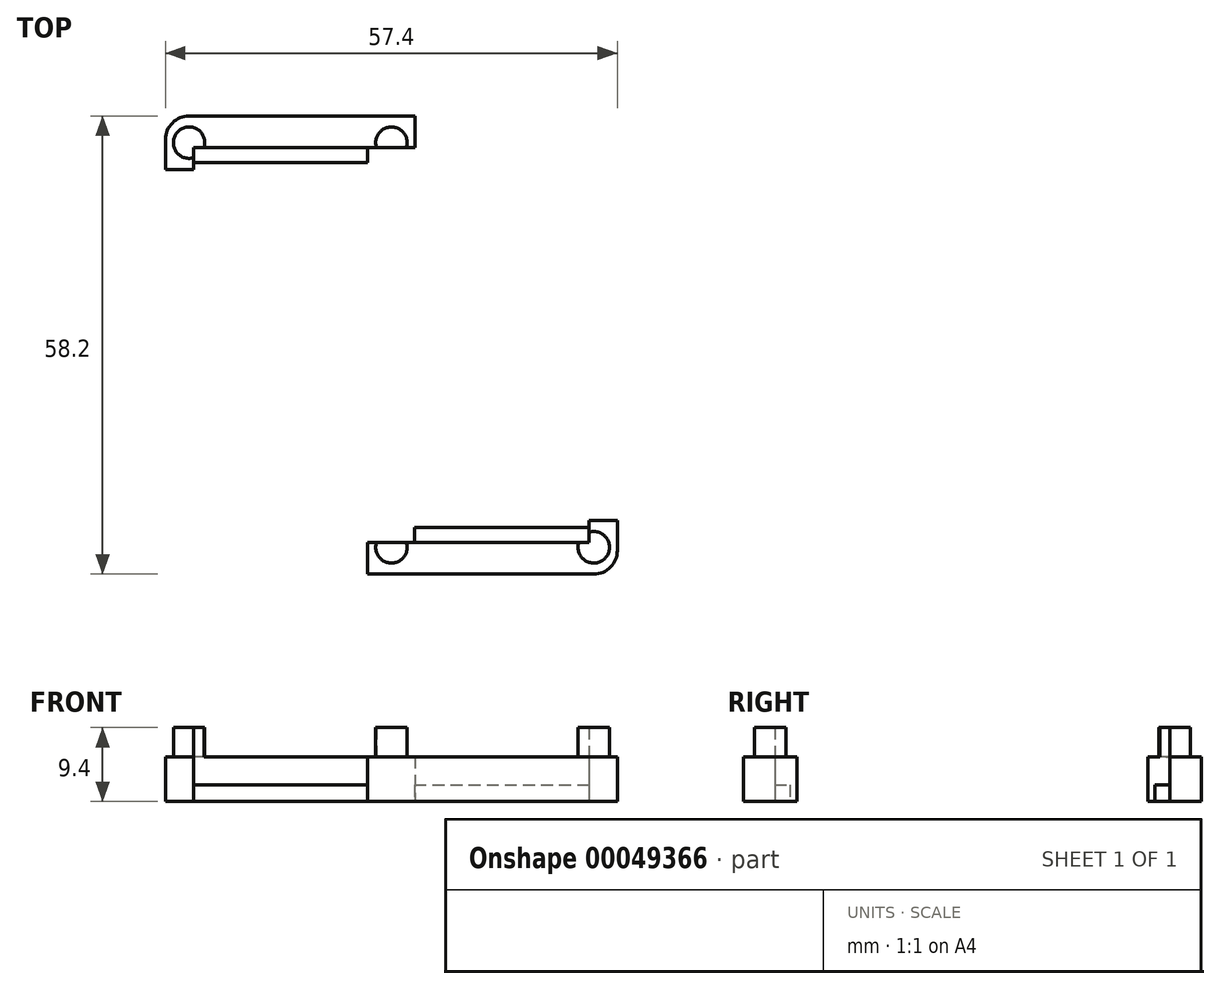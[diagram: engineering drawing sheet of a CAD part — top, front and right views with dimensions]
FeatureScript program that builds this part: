
annotation { "Feature Type Name" : "Feature", "Feature Type Description" : "" }
export const myFeature = defineFeature(function(context is Context, id is Id, definition is map)
    precondition{}
    {
        {
            var Q0;
            Q0=qCreatedBy(makeId("Top.planeOp"),FACE);
            var sketch = newSketch(context, id + "F0", { "sketchPlane" : qUnion([Q0])});
            skLineSegment(sketch, "E0.rect.top", {"start": v(24.8, 24.8) * mm, "end": v(24.03, 24.8) * mm});
            skLineSegment(sketch, "E0.rect.right", {"start": v(-24.8, -24.8) * mm, "end": v(-24.8, 22.3) * mm});
            skPoint(sketch, "E0.rect.middle", {"position": v(0, 0) * mm});
            skCircle(sketch, "E1", {"center": v(0, 0) * mm, "radius": 1.9 * mm});
            skCircle(sketch, "E2", {"center": v(25.7, 0) * mm, "radius": 1.9 * mm});
            skCircle(sketch, "E3", {"center": v(25.7, 25.7) * mm, "radius": 1.9 * mm});
            skPoint(sketch, "E4.MirrorP", {"position": v(0, 25.7) * mm});
            skCircle(sketch, "E5.MirrorC", {"center": v(-25.7, 0) * mm, "radius": 1.9 * mm});
            skArc(sketch, "E6.MirrorC", {"start": v(1.67, 24.8) * mm, "mid": v(0.16, 27.6) * mm, "end": v(-1.8, 25.1) * mm});
            skCircle(sketch, "E7.MirrorC", {"center": v(-25.7, -25.7) * mm, "radius": 1.9 * mm});
            skPoint(sketch, "E8.MirrorP", {"position": v(0, -25.7) * mm});
            skLineSegment(sketch, "E9.MirrorCS", {"start": v(-24.8, -24.8) * mm, "end": v(-3, -24.8) * mm});
            skLineSegment(sketch, "E10.MirrorCS", {"start": v(-3, -24.8) * mm, "end": v(-24.8, -24.8) * mm});
            skPoint(sketch, "E11.MirrorCS.end.orphan", {"position": v(-28.25, 12.85) * mm});
            skPoint(sketch, "E12.orphan", {"position": v(-25.7, 12.85) * mm});
            skPoint(sketch, "E13.endSnap0", {"position": v(0, -24.8) * mm});
            skLineSegment(sketch, "E14.rect.bottom", {"start": v(24.8, -22.3) * mm, "end": v(28.7, -22.3) * mm});
            skLineSegment(sketch, "E14.rect.top", {"start": v(-3, -29.1) * mm, "end": v(28.7, -29.1) * mm});
            skLineSegment(sketch, "E14.rect.left", {"start": v(-3, -24.8) * mm, "end": v(-3, -29.1) * mm});
            skLineSegment(sketch, "E14.rect.right", {"start": v(28.7, -22.3) * mm, "end": v(28.7, -29.1) * mm});
            skPoint(sketch, "E14.rect.middle", {"position": v(12.85, -25.7) * mm});
            skArc(sketch, "E15.MirrorCS", {"start": v(24.03, 24.8) * mm, "mid": v(27.04, 27.04) * mm, "end": v(24.8, 24.03) * mm});
            skArc(sketch, "E16.MirrorCS", {"start": v(24.8, 24.03) * mm, "mid": v(27.04, 27.04) * mm, "end": v(24.03, 24.8) * mm});
            skPoint(sketch, "E17.MirrorP", {"position": v(12.85, 25.7) * mm});
            skLineSegment(sketch, "E18.MirrorCS", {"start": v(-3, 29.1) * mm, "end": v(3, 29.1) * mm});
            skPoint(sketch, "E19.MirrorP", {"position": v(0, 24.8) * mm});
            skArc(sketch, "E20.MirrorC", {"start": v(1.8, 25.1) * mm, "mid": v(1.74, 24.95) * mm, "end": v(1.67, 24.8) * mm});
            skLineSegment(sketch, "E21.MirrorCS", {"start": v(-28.7, 22.3) * mm, "end": v(-28.7, 29.1) * mm});
            skLineSegment(sketch, "E22.MirrorCS", {"start": v(3, 29.1) * mm, "end": v(-28.7, 29.1) * mm});
            skLineSegment(sketch, "E23.MirrorCS", {"start": v(3, 24.8) * mm, "end": v(3, 29.1) * mm});
            skPoint(sketch, "E24.MirrorP", {"position": v(-12.85, 25.7) * mm});
            skArc(sketch, "E25.MirrorCS", {"start": v(1.67, 24.8) * mm, "mid": v(1.74, 24.95) * mm, "end": v(1.8, 25.1) * mm});
            skPoint(sketch, "E26.MirrorCS.end.orphan", {"position": v(28.7, 29.1) * mm});
            skPoint(sketch, "E27.orphan", {"position": v(28.7, 22.3) * mm});
            skPoint(sketch, "E28.end.orphan", {"position": v(-3.94, -25.7) * mm});
            skLineSegment(sketch, "E29", {"start": v(-3, -25.1) * mm, "end": v(-2.61, -25.1) * mm});
            skLineSegment(sketch, "E30", {"start": v(-2.61, -25.1) * mm, "end": v(25.13, -25.1) * mm});
            skLineSegment(sketch, "E31", {"start": v(25.13, -25.1) * mm, "end": v(25.13, -22.3) * mm});
            skLineSegment(sketch, "E32.trimOffspring", {"start": v(24.8, -22.3) * mm, "end": v(24.8, 24.8) * mm});
            skPoint(sketch, "E33.orphan", {"position": v(24.8, -24.03) * mm});
            skPoint(sketch, "E34.MirrorC.start.orphan", {"position": v(24.03, -24.8) * mm});
            skPoint(sketch, "E0.rect.bottom.start.orphan", {"position": v(24.8, -24.8) * mm});
            skPoint(sketch, "E35.orphan", {"position": v(-1.67, -24.8) * mm});
            skPoint(sketch, "E36.orphan", {"position": v(1.67, -24.8) * mm});
            skLineSegment(sketch, "E37", {"start": v(3, 25.1) * mm, "end": v(-25.12, 25.1) * mm});
            skLineSegment(sketch, "E38", {"start": v(-25.12, 25.1) * mm, "end": v(-25.12, 22.3) * mm});
            skPoint(sketch, "E39.orphan", {"position": v(-24.8, 24.8) * mm});
            skPoint(sketch, "E40.orphan", {"position": v(-24.8, 24.03) * mm});
            skPoint(sketch, "E41.MirrorC.center.orphan", {"position": v(-25.7, 25.7) * mm});
            skPoint(sketch, "E42.MirrorCS.end.orphan", {"position": v(-24.03, 24.8) * mm});
            skPoint(sketch, "E43.orphan", {"position": v(-1.67, 24.8) * mm});
            skLineSegment(sketch, "E44.trimOffspring", {"start": v(3, 24.8) * mm, "end": v(24.8, 24.8) * mm});
            skPoint(sketch, "E45.end.orphan", {"position": v(2.6, 25.1) * mm});
            skArc(sketch, "E46", {"start": v(-23.8, 25.1) * mm, "mid": v(-27.1, 27.12) * mm, "end": v(-25.12, 23.79) * mm});
            skCircle(sketch, "E47", {"center": v(0, 25.7) * mm, "radius": 2 * mm});
            skArc(sketch, "E48", {"start": v(-1.9, -25.1) * mm, "mid": v(0, -27.7) * mm, "end": v(1.9, -25.1) * mm});
            skArc(sketch, "E49", {"start": v(23.8, -25.1) * mm, "mid": v(27.1, -27.12) * mm, "end": v(25.13, -23.78) * mm});
            skLineSegment(sketch, "E50", {"start": v(2.92, -23.2) * mm, "end": v(25.13, -23.2) * mm});
            skLineSegment(sketch, "E51", {"start": v(2.92, -25.1) * mm, "end": v(2.92, -23.2) * mm});
            skPoint(sketch, "E52.start.orphan", {"position": v(-4.43, -22.3) * mm});
            skPoint(sketch, "E53.start.orphan", {"position": v(0, -22.3) * mm});
            skPoint(sketch, "E54.orphan", {"position": v(-3, -22.3) * mm});
            skLineSegment(sketch, "E55", {"start": v(-3, 23.2) * mm, "end": v(-3, 25.1) * mm});
            skLineSegment(sketch, "E56.trimOffspring", {"start": v(-24.8, 22.3) * mm, "end": v(-28.7, 22.3) * mm});
            skLineSegment(sketch, "E57.trimOffspring", {"start": v(-3, 23.2) * mm, "end": v(-25.12, 23.2) * mm});
            skPoint(sketch, "E58.start.orphan", {"position": v(4.08, 22.3) * mm});
            skPoint(sketch, "E59.MirrorCS.start.orphan", {"position": v(0, 22.3) * mm});
            skPoint(sketch, "E60.orphan", {"position": v(-3, 22.3) * mm});
            skPoint(sketch, "E61.MirrorCS.start.orphan", {"position": v(3, 22.3) * mm});
            skSolve(sketch);
        }
        {
            var Q0;
            {var subQ0=sQuery(id+"F0.wireOp",EDGE,"E49");Q0=makeQuery(id+"F0.imprint","IMPRINT",FACE,{"disambiguationData":[TD([[makeQuery(id+"F0.imprint","IMPRINT",EDGE,{"derivedFrom":subQ0}),1.0]])]});}
            var Q1;
            {var subQ0=sQuery(id+"F0.wireOp",EDGE,"E48");Q1=makeQuery(id+"F0.imprint","IMPRINT",FACE,{"disambiguationData":[TD([[makeQuery(id+"F0.imprint","IMPRINT",EDGE,{"derivedFrom":subQ0}),1.0]])]});}
            var Q2;
            {var subQ0=sQuery(id+"F0.wireOp",EDGE,"E46");Q2=makeQuery(id+"F0.imprint","IMPRINT",FACE,{"disambiguationData":[TD([[makeQuery(id+"F0.imprint","IMPRINT",EDGE,{"derivedFrom":subQ0}),1.0]])]});}
            var Q3;
            {var subQ1=sQuery(id+"F0.wireOp",EDGE,"E6.MirrorC");Q3=makeQuery(id+"F0.imprint","IMPRINT",FACE,{"disambiguationData":[TD([[makeQuery(id+"F0.imprint","IMPRINT",EDGE,{"derivedFrom":subQ1}),1.0]])]});}
            var Q4;
            {var subQ4=sQuery(id+"F0.wireOp",EDGE,"E6.MirrorC");Q4=makeQuery(id+"F0.imprint","IMPRINT",FACE,{"disambiguationData":[TD([[makeQuery(id+"F0.imprint","IMPRINT",EDGE,{"derivedFrom":subQ4}),-1.0]])]});}
            extrude(context, id + "F1", {"entities" : qUnion([Q0, Q1, Q2, Q3, Q4]), "depth" : 9.4 * mm});
        }
        {
            var Q0;
            {var subQ8=sQuery(id+"F0.wireOp",EDGE,"E14.rect.top");Q0=makeQuery(id+"F0.imprint","IMPRINT",FACE,{"disambiguationData":[TD([[makeQuery(id+"F0.imprint","IMPRINT",EDGE,{"derivedFrom":subQ8}),1.0]])]});}
            var Q1;
            {var subQ12=sQuery(id+"F0.wireOp",EDGE,"E21.MirrorCS");Q1=makeQuery(id+"F0.imprint","IMPRINT",FACE,{"disambiguationData":[TD([[makeQuery(id+"F0.imprint","IMPRINT",EDGE,{"derivedFrom":subQ12}),-1.0]])]});}
            extrude(context, id + "F2", {"entities" : qUnion([Q0, Q1]), "operationType" : NewBodyOperationType.ADD, "depth" : 5.7 * mm});
        }
        {
            var Q0;
            {var subQ1=sQuery(id+"F0.wireOp",EDGE,"E55");Q0=makeQuery(id+"F0.imprint","IMPRINT",FACE,{"disambiguationData":[TD([[makeQuery(id+"F0.imprint","IMPRINT",EDGE,{"derivedFrom":subQ1}),1.0]])]});}
            var Q1;
            {var subQ1=sQuery(id+"F0.wireOp",EDGE,"E50");Q1=makeQuery(id+"F0.imprint","IMPRINT",FACE,{"disambiguationData":[TD([[makeQuery(id+"F0.imprint","IMPRINT",EDGE,{"derivedFrom":subQ1}),-1.0]])]});}
            extrude(context, id + "F3", {"entities" : qUnion([Q0, Q1]), "operationType" : NewBodyOperationType.ADD, "depth" : 2.1 * mm});
        }
        {
            var Q0;
            Q0=makeQuery(id+"F2.opExtrude","SWEPT_EDGE",EDGE,{"disambiguationData":[OSD([sQuery(id+"F0.wireOp",EDGE,"E14.rect.top"),sQuery(id+"F0.wireOp",EDGE,"E14.rect.right")])]});
            var Q1;
            Q1=makeQuery(id+"F2.opExtrude","SWEPT_EDGE",EDGE,{"disambiguationData":[OSD([sQuery(id+"F0.wireOp",EDGE,"E21.MirrorCS"),sQuery(id+"F0.wireOp",EDGE,"E22.MirrorCS")])]});
            fillet(context, id + "F4", {"entities" : qUnion([Q0, Q1]), "radius" : 3 * mm, "tangentPropagation" : true, "allowEdgeOverflow" : false});
        }
    });
